# Revit family: StructuralConnector_CastConnex_UPC_EN_20240923
name_source: partatom
category: Structural Connections
units: mm (PartAtom-declared; Revit-internal decimal feet)

## family parameters
Cut with Voids When Loaded = No
Enable Cutting in Views = Yes
Host = Face
Material for Model Behavior = Other
OmniClass Number = 23.25.30.11
OmniClass Title = Structural Frames
Shared = No

## types (10) — shared parameters
Assembly Code = B1010200
Default Elevation = 101.6 mm
Description = Structural Connector - CAST CONNEX UPC-4.000L Universal Pin Connector
Keynote = 05 12 00
Manufacturer = CAST CONNEX
Model = UPC-4.000L
UPC = Material and Finish as Specified
URL = https://www.castconnex.com

## per-type parameters (varying)
| type | D | D pin | G | G' | L | TipLoc | W | W1 | X1 | X2 | X3 | X4 | e | eg_max | j | te | tf |
| UPC(EN)-89 | 88.9 mm | 32 mm | 22 mm | 22 mm | 215 mm | 20.8 mm | 84 mm | 42 mm  [stored 0.137795 ft] | 16 mm  [stored 0.0524934 ft] | 4 mm  [stored 0.0131234 ft] | 7 mm | 53.7 mm | 54 mm | 72 mm | 12 mm  [stored 0.0393701 ft] | 15 mm | 18 mm |
| UPC(EN)-114 | 114.3 mm | 42 mm  [stored 0.137795 ft] | 27 mm | 27 mm | 275 mm | 26 mm | 108 mm | 54 mm | 21 mm | 5 mm  [stored 0.0164042 ft] | 9 mm | 68.7 mm | 69 mm | 92 mm | 15 mm | 20 mm  [stored 0.0656168 ft] | 23 mm |
| UPC(EN)-140 | 139.7 mm | 50 mm | 27 mm | 37 mm | 340 mm | 26 mm | 132 mm | 66 mm | 25 mm  [stored 0.082021 ft] | 5 mm  [stored 0.0164042 ft] | 9 mm | 85.3 mm | 84 mm | 116 mm | 15 mm | 20 mm  [stored 0.0656168 ft] | 24 mm |
| UPC(EN)-168 | 168.3 mm | 60 mm | 32 mm | 42 mm  [stored 0.137795 ft] | 405 mm | 26 mm | 159 mm | 79.5 mm | 30 mm | 6 mm | 10 mm  [stored 0.0328084 ft] | 101.3 mm | 101 mm | 136 mm | 15 mm | 20 mm  [stored 0.0656168 ft] | 28 mm |
| UPC(EN)-194 | 193.7 mm | 70 mm | 37 mm | 47 mm | 465 mm | 34.6 mm | 183 mm | 91.5 mm | 35 mm | 7 mm | 12 mm  [stored 0.0393701 ft] | 116.3 mm | 116 mm | 155 mm | 20 mm  [stored 0.0656168 ft] | 25 mm  [stored 0.082021 ft] | 33 mm  [stored 0.108268 ft] |
| UPC(EN)-219 | 219.1 mm | 75 mm | 42 mm  [stored 0.137795 ft] | 52 mm | 515 mm | 34.6 mm | 205 mm | 102.5 mm | 37.5 mm | 7 mm | 12 mm  [stored 0.0393701 ft] | 128.7 mm | 129 mm | 167 mm | 20 mm  [stored 0.0656168 ft] | 25 mm  [stored 0.082021 ft] | 33 mm  [stored 0.108268 ft] |
| UPC(EN)-273 | 273.1 mm | 90 mm | 52 mm | 72 mm | 630 mm | 34.6 mm | 258 mm | 129 mm | 45 mm | 7 mm | 13 mm | 156.7 mm | 160 mm | 197 mm | 20 mm  [stored 0.0656168 ft] | 25 mm  [stored 0.082021 ft] | 35 mm |
| UPC(EN)-324 | 323.9 mm | 100 mm | 57 mm | 77 mm | 725 mm | 34.6 mm | 299 mm | 149.5 mm | 50 mm | 7 mm | 13 mm | 180.3 mm | 184 mm | 217 mm | 20 mm  [stored 0.0656168 ft] | 25 mm  [stored 0.082021 ft] | 35 mm |
| UPC(EN)-356 | 355.6 mm | 110 mm | 57 mm | 77 mm | 795 mm | 34.6 mm | 328 mm | 164 mm | 55 mm | 7 mm | 13 mm | 197.7 mm | 202 mm | 237 mm | 20 mm  [stored 0.0656168 ft] | 25 mm  [stored 0.082021 ft] | 35 mm |
| UPC(EN)-406 | 406.4 mm | 115 mm | 62 mm | 82 mm | 875 mm | 34.6 mm | 356 mm | 178 mm | 57.5 mm  [stored 0.188648 ft] | 7 mm | 13 mm | 219 mm | 218 mm | 251 mm | 20 mm  [stored 0.0656168 ft] | 25 mm  [stored 0.082021 ft] | 35 mm |

note: [stored X ft] marks values corroborated as IEEE doubles in the binary element streams (Revit-internal decimal feet)

## geometry (parser evidence)
native form markers: Sweep x3
no freeform markers — native parametric forms only
